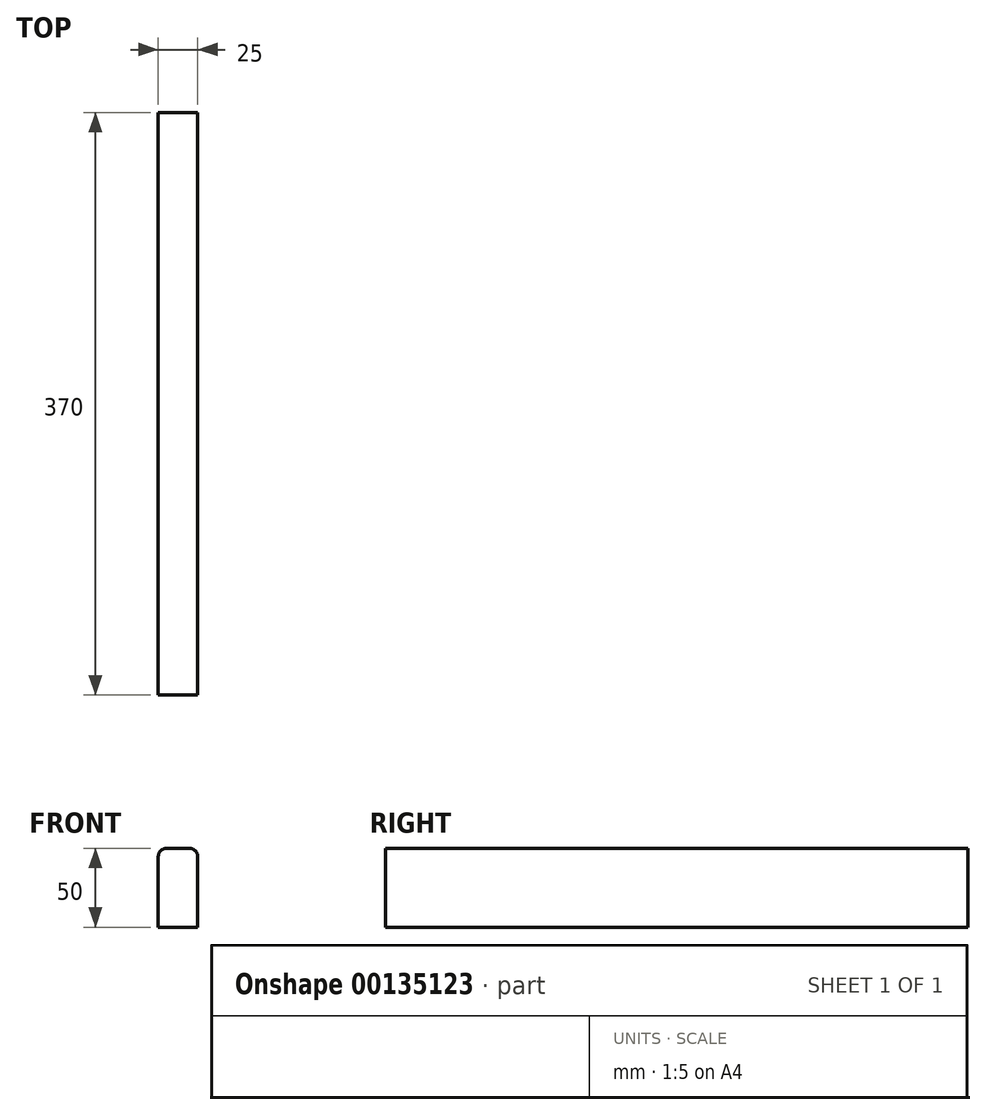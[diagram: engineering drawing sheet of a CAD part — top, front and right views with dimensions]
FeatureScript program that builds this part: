
annotation { "Feature Type Name" : "Feature", "Feature Type Description" : "" }
export const myFeature = defineFeature(function(context is Context, id is Id, definition is map)
    precondition{}
    {
        {
            var Q0;
            Q0=qCreatedBy(makeId("Front.planeOp"),FACE);
            var sketch = newSketch(context, id + "F0", { "sketchPlane" : qUnion([Q0])});
            skLineSegment(sketch, "E0.bottom", {"start": v(0, 0) * mm, "end": v(25, 0) * mm});
            skLineSegment(sketch, "E0.top", {"start": v(5, 50) * mm, "end": v(20, 50) * mm});
            skLineSegment(sketch, "E0.left", {"start": v(0, 0) * mm, "end": v(0, 45) * mm});
            skLineSegment(sketch, "E0.right", {"start": v(25, 0) * mm, "end": v(25, 45) * mm});
            skPoint(sketch, "E1.visualSharp", {"position": v(0, 50) * mm});
            skArc(sketch, "E1.filletArc", {"start": v(5, 50) * mm, "mid": v(1.46, 48.54) * mm, "end": v(0, 45) * mm});
            skPoint(sketch, "E2.visualSharp", {"position": v(25, 50) * mm});
            skArc(sketch, "E2.filletArc", {"start": v(25, 45) * mm, "mid": v(23.54, 48.54) * mm, "end": v(20, 50) * mm});
            skSolve(sketch);
        }
        {
            var Q0;
            Q0=qSketchRegion(id+"F0",true);
            extrude(context, id + "F1", {"entities" : qUnion([Q0]), "depth" : 370 * mm});
        }
    });
